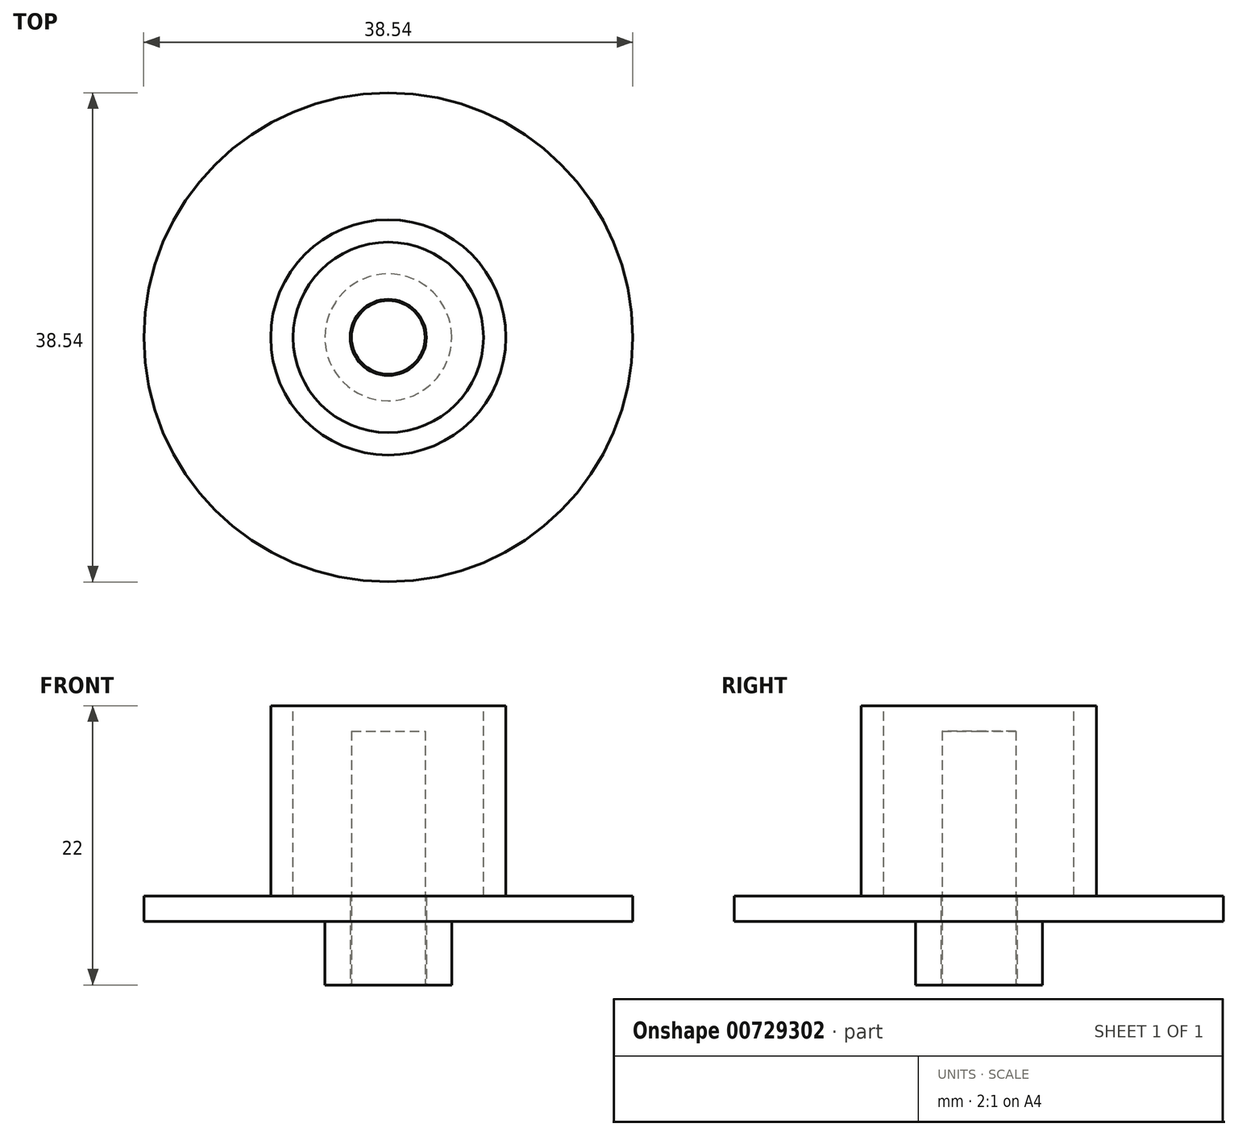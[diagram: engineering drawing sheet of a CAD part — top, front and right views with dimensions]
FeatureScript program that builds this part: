
annotation { "Feature Type Name" : "Feature", "Feature Type Description" : "" }
export const myFeature = defineFeature(function(context is Context, id is Id, definition is map)
    precondition{}
    {
        {
            var Q0;
            Q0=qCreatedBy(makeId("Front.planeOp"),FACE);
            var sketch = newSketch(context, id + "F0", { "sketchPlane" : qUnion([Q0])});
            skLineSegment(sketch, "E0", {"start": v(0, 0) * mm, "end": v(9.27, 0) * mm});
            skLineSegment(sketch, "E1", {"start": v(9.27, 0) * mm, "end": v(9.27, -15) * mm});
            skLineSegment(sketch, "E2", {"start": v(9.27, -15) * mm, "end": v(19.27, -15) * mm});
            skLineSegment(sketch, "E3", {"start": v(19.27, -15) * mm, "end": v(19.27, -17) * mm});
            skLineSegment(sketch, "E4", {"start": v(19.27, -17) * mm, "end": v(9.27, -17) * mm});
            skLineSegment(sketch, "E5", {"start": v(9.27, -17) * mm, "end": v(5, -17) * mm});
            skLineSegment(sketch, "E6", {"start": v(5, -17) * mm, "end": v(5, -22) * mm});
            skLineSegment(sketch, "E7", {"start": v(5, -22) * mm, "end": v(0, -22) * mm});
            skLineSegment(sketch, "E8", {"start": v(0, -22) * mm, "end": v(0, 0) * mm});
            skSolve(sketch);
        }
        {
            var Q0;
            Q0=qSketchRegion(id+"F0",true);
            var Q1;
            Q1=sQuery(id+"F0.wireOp",EDGE,"E8");
            revolve(context, id + "F1", {"surfaceOperationType" : NewSurfaceOperationType.NEW, "entities" : qUnion([Q0]), "axis" : qUnion([Q1]), "revolveType" : RevolveType.FULL});
        }
        {
            var Q0;
            Q0=makeQuery(id+"F1.opRevolve","SWEPT_FACE",FACE,{"disambiguationData":[OSD([sQuery(id+"F0.wireOp",EDGE,"E0")])]});
            var sketch = newSketch(context, id + "F2", { "sketchPlane" : qUnion([Q0])});
            skCircle(sketch, "E9", {"center": v(0, 0) * mm, "radius": 7.5 * mm});
            skSolve(sketch);
        }
        {
            var Q0;
            Q0=qSketchRegion(id+"F2",true);
            var Q1;
            Q1=makeQuery(id+"F1.opRevolve","SWEPT_FACE",FACE,{"disambiguationData":[OSD([sQuery(id+"F0.wireOp",EDGE,"E2")])]});
            extrude(context, id + "F3", {"entities" : qUnion([Q0]), "operationType" : NewBodyOperationType.REMOVE, "endBound" : BoundingType.UP_TO_SURFACE, "oppositeDirection" : true, "depth" : 25 * mm, "endBoundEntityFace" : qUnion([Q1]), "offsetDistance" : 25 * mm});
        }
        {
            var Q0;
            Q0=makeQuery(id+"F1.opRevolve","SWEPT_FACE",FACE,{"disambiguationData":[OSD([sQuery(id+"F0.wireOp",EDGE,"E7")])]});
            var sketch = newSketch(context, id + "F4", { "sketchPlane" : qUnion([Q0])});
            skCircle(sketch, "E10", {"center": v(0, 0) * mm, "radius": 3 * mm});
            skSolve(sketch);
        }
        {
            var Q0;
            Q0=qSketchRegion(id+"F4",true);
            extrude(context, id + "F5", {"entities" : qUnion([Q0]), "operationType" : NewBodyOperationType.REMOVE, "endBound" : BoundingType.THROUGH_ALL, "oppositeDirection" : true, "depth" : 25 * mm, "offsetDistance" : 25 * mm});
        }
        {
            var Q0;
            Q0=makeQuery(id+"F1.opRevolve","SWEPT_FACE",FACE,{"disambiguationData":[OSD([sQuery(id+"F0.wireOp",EDGE,"E7")])]});
            var sketch = newSketch(context, id + "F6", { "sketchPlane" : qUnion([Q0])});
            skCircle(sketch, "E11", {"center": v(0, 0) * mm, "radius": 2.9 * mm});
            skSolve(sketch);
        }
        {
            var Q0;
            Q0=qSketchRegion(id+"F6",true);
            extrude(context, id + "F7", {"entities" : qUnion([Q0]), "oppositeDirection" : true, "depth" : 20 * mm, "offsetDistance" : 25 * mm});
        }
    });
